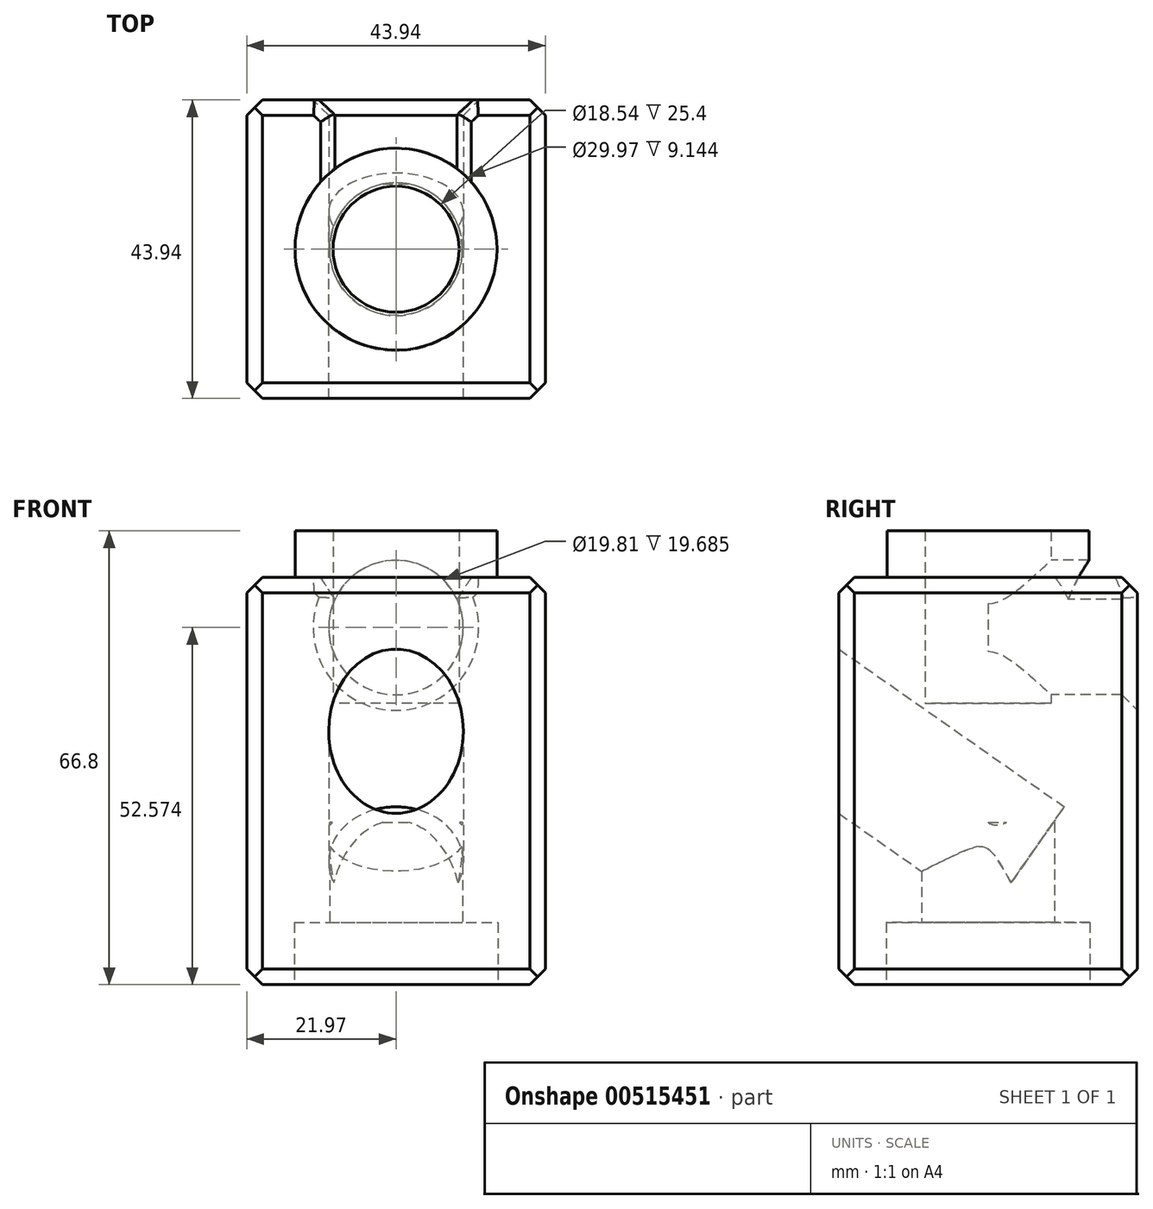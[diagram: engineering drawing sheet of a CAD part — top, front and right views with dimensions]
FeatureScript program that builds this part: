
annotation { "Feature Type Name" : "Feature", "Feature Type Description" : "" }
export const myFeature = defineFeature(function(context is Context, id is Id, definition is map)
    precondition{}
    {
        {
            var Q0;
            Q0=qCreatedBy(makeId("Top.planeOp"),FACE);
            var sketch = newSketch(context, id + "F0", { "sketchPlane" : qUnion([Q0])});
            skCircle(sketch, "E0", {"center": v(0, 0) * mm, "radius": 14.86 * mm});
            skCircle(sketch, "E1", {"center": v(0, 0) * mm, "radius": 9.27 * mm});
            skSolve(sketch);
        }
        {
            var Q0;
            Q0 = qSketchRegion(id + "F0", true);
            extrude(context, id + "F1", {"entities" : qUnion([Q0]), "depth" : 6.86 * mm, "offsetDistance" : 25.4 * mm});
        }
        {
            var Q0;
            Q0=qCreatedBy(makeId("Top.planeOp"),FACE);
            var sketch = newSketch(context, id + "F2", { "sketchPlane" : qUnion([Q0])});
            skLineSegment(sketch, "E2.bottom", {"start": v(-21.97, 21.97) * mm, "end": v(21.97, 21.97) * mm});
            skLineSegment(sketch, "E2.top", {"start": v(-21.97, -21.97) * mm, "end": v(21.97, -21.97) * mm});
            skLineSegment(sketch, "E2.left", {"start": v(-21.97, 21.97) * mm, "end": v(-21.97, -21.97) * mm});
            skLineSegment(sketch, "E2.right", {"start": v(21.97, 21.97) * mm, "end": v(21.97, -21.97) * mm});
            skPoint(sketch, "E2.middle", {"position": v(0, 0) * mm});
            skSolve(sketch);
        }
        {
            var Q0;
            Q0 = qSketchRegion(id + "F2", true);
            extrude(context, id + "F3", {"entities" : qUnion([Q0]), "operationType" : NewBodyOperationType.ADD, "oppositeDirection" : true, "depth" : 59.94 * mm, "offsetDistance" : 25.4 * mm});
        }
        {
            var Q0;
            Q0=makeQuery(id+"F3.boolean.opBoolean","SPLIT",FACE,{"disambiguationData":[TD([makeQuery(id+"F1.opExtrude","SWEPT_FACE",FACE,{"disambiguationData":[OSD([sQuery(id+"F0.wireOp",EDGE,"E1")])]})])],"derivedFrom":makeQuery(id+"F3.opExtrude","CAP_FACE",FACE,{"disambiguationData":[OSD([sQuery(id+"F2.wireOp",EDGE,"E2.bottom"),sQuery(id+"F2.wireOp",EDGE,"E2.top"),sQuery(id+"F2.wireOp",EDGE,"E2.left"),sQuery(id+"F2.wireOp",EDGE,"E2.right")])],"isStart":true})});
            extrude(context, id + "F4", {"entities" : qUnion([Q0]), "operationType" : NewBodyOperationType.REMOVE, "oppositeDirection" : true, "depth" : 18.54 * mm, "offsetDistance" : 25.4 * mm});
        }
        {
            var Q0;
            Q0=makeQuery(id+"F3.opExtrude","SWEPT_EDGE",EDGE,{"disambiguationData":[OSD([sQuery(id+"F2.wireOp",EDGE,"E2.bottom"),sQuery(id+"F2.wireOp",EDGE,"E2.left")])]});
            chamfer(context, id + "F5", {"entities" : qUnion([Q0]), "width" : 2.3 * mm, "tangentPropagation" : true});
        }
        {
            var Q0;
            Q0=makeQuery(id+"F3.opExtrude","SWEPT_EDGE",EDGE,{"disambiguationData":[OSD([sQuery(id+"F2.wireOp",EDGE,"E2.top"),sQuery(id+"F2.wireOp",EDGE,"E2.left")])]});
            var Q1;
            Q1=makeQuery(id+"F3.opExtrude","SWEPT_EDGE",EDGE,{"disambiguationData":[OSD([sQuery(id+"F2.wireOp",EDGE,"E2.bottom"),sQuery(id+"F2.wireOp",EDGE,"E2.right")])]});
            chamfer(context, id + "F6", {"entities" : qUnion([Q0, Q1]), "width" : 2.3 * mm, "tangentPropagation" : true});
        }
        {
            var Q0;
            Q0=makeQuery(id+"F3.opExtrude","SWEPT_EDGE",EDGE,{"disambiguationData":[OSD([sQuery(id+"F2.wireOp",EDGE,"E2.top"),sQuery(id+"F2.wireOp",EDGE,"E2.right")])]});
            chamfer(context, id + "F7", {"entities" : qUnion([Q0]), "width" : 2.3 * mm, "tangentPropagation" : true});
        }
        {
            var Q0;
            Q0=qCreatedBy(makeId("Front.planeOp"),FACE);
            var sketch = newSketch(context, id + "F8", { "sketchPlane" : qUnion([Q0])});
            skCircle(sketch, "E3", {"center": v(0, -7.37) * mm, "radius": 9.9 * mm});
            skSolve(sketch);
        }
        {
            var Q0;
            Q0 = qSketchRegion(id + "F8", true);
            extrude(context, id + "F9", {"entities" : qUnion([Q0]), "operationType" : NewBodyOperationType.REMOVE, "oppositeDirection" : true, "depth" : 25.4 * mm, "offsetDistance" : 25.4 * mm});
        }
        {
            var Q0;
            Q0=makeQuery(id+"F9.boolean.opBoolean","INTERSECT",EDGE,{"derivedFrom":[makeQuery(id+"F3.opExtrude","SWEPT_FACE",FACE,{"disambiguationData":[OSD([sQuery(id+"F2.wireOp",EDGE,"E2.bottom")])]}),makeQuery(id+"F9.opExtrude","SWEPT_FACE",FACE,{"disambiguationData":[OSD([sQuery(id+"F8.wireOp",EDGE,"E3")])]})]});
            chamfer(context, id + "F10", {"entities" : qUnion([Q0]), "width" : 2.3 * mm, "tangentPropagation" : true});
        }
        {
            var Q0;
            {var subQ0=sQuery(id+"F2.wireOp",EDGE,"E2.left");var subQ1=sQuery(id+"F2.wireOp",EDGE,"E2.top");var subQ2=sQuery(id+"F2.wireOp",EDGE,"E2.bottom");var subQ3=sQuery(id+"F2.wireOp",EDGE,"E2.right");Q0=makeQuery(id+"F9.boolean.opBoolean","INTERSECT",EDGE,{"disambiguationData":[OD(1.0)],"derivedFrom":[makeQuery(id+"F3.boolean.opBoolean","SPLIT",FACE,{"disambiguationData":[TD([makeQuery(id+"F1.opExtrude","SWEPT_FACE",FACE,{"disambiguationData":[OSD([sQuery(id+"F0.wireOp",EDGE,"E0")])]})])],"derivedFrom":makeQuery(id+"F3.opExtrude","CAP_FACE",FACE,{"disambiguationData":[OSD([subQ2,subQ1,subQ0,subQ3])],"isStart":true})}),makeQuery(id+"F9.opExtrude","SWEPT_FACE",FACE,{"disambiguationData":[OSD([sQuery(id+"F8.wireOp",EDGE,"E3")])]})]});}
            var Q1;
            {var subQ0=sQuery(id+"F2.wireOp",EDGE,"E2.left");var subQ1=sQuery(id+"F2.wireOp",EDGE,"E2.top");var subQ2=sQuery(id+"F2.wireOp",EDGE,"E2.bottom");var subQ3=sQuery(id+"F2.wireOp",EDGE,"E2.right");Q1=makeQuery(id+"F9.boolean.opBoolean","INTERSECT",EDGE,{"disambiguationData":[OD(0.0)],"derivedFrom":[makeQuery(id+"F3.boolean.opBoolean","SPLIT",FACE,{"disambiguationData":[TD([makeQuery(id+"F1.opExtrude","SWEPT_FACE",FACE,{"disambiguationData":[OSD([sQuery(id+"F0.wireOp",EDGE,"E0")])]})])],"derivedFrom":makeQuery(id+"F3.opExtrude","CAP_FACE",FACE,{"disambiguationData":[OSD([subQ2,subQ1,subQ0,subQ3])],"isStart":true})}),makeQuery(id+"F9.opExtrude","SWEPT_FACE",FACE,{"disambiguationData":[OSD([sQuery(id+"F8.wireOp",EDGE,"E3")])]})]});}
            var Q2;
            {var subQ0=sQuery(id+"F2.wireOp",EDGE,"E2.left");var subQ1=sQuery(id+"F2.wireOp",EDGE,"E2.top");var subQ2=sQuery(id+"F2.wireOp",EDGE,"E2.bottom");var subQ3=makeQuery(id+"F3.opExtrude","SWEPT_FACE",FACE,{"disambiguationData":[OSD([subQ2])]});var subQ4=sQuery(id+"F2.wireOp",EDGE,"E2.right");Q2=makeQuery(id+"F10.opChamfer","BLEND_EDGE",EDGE,{"disambiguationData":[OD(0.0)],"blendedFrom":[makeQuery(id+"F9.boolean.opBoolean","INTERSECT",EDGE,{"derivedFrom":[subQ3,makeQuery(id+"F9.opExtrude","SWEPT_FACE",FACE,{"disambiguationData":[OSD([sQuery(id+"F8.wireOp",EDGE,"E3")])]})]}),makeQuery(id+"F3.boolean.opBoolean","SPLIT",FACE,{"disambiguationData":[TD([makeQuery(id+"F1.opExtrude","SWEPT_FACE",FACE,{"disambiguationData":[OSD([sQuery(id+"F0.wireOp",EDGE,"E0")])]})])],"derivedFrom":makeQuery(id+"F3.opExtrude","CAP_FACE",FACE,{"disambiguationData":[OSD([subQ2,subQ1,subQ0,subQ4])],"isStart":true})})],"blendedInto":[makeQuery(id+"F3.boolean.opBoolean","SPLIT",FACE,{"disambiguationData":[TD([makeQuery(id+"F1.opExtrude","SWEPT_FACE",FACE,{"disambiguationData":[OSD([sQuery(id+"F0.wireOp",EDGE,"E0")])]})])],"derivedFrom":makeQuery(id+"F3.opExtrude","CAP_FACE",FACE,{"disambiguationData":[OSD([subQ2,subQ1,subQ0,subQ4])],"isStart":true})})]});}
            var Q3;
            {var subQ0=sQuery(id+"F2.wireOp",EDGE,"E2.left");var subQ1=sQuery(id+"F2.wireOp",EDGE,"E2.top");var subQ2=sQuery(id+"F2.wireOp",EDGE,"E2.bottom");var subQ3=makeQuery(id+"F3.opExtrude","SWEPT_FACE",FACE,{"disambiguationData":[OSD([subQ2])]});var subQ4=sQuery(id+"F2.wireOp",EDGE,"E2.right");Q3=makeQuery(id+"F10.opChamfer","BLEND_EDGE",EDGE,{"disambiguationData":[OD(1.0)],"blendedFrom":[makeQuery(id+"F9.boolean.opBoolean","INTERSECT",EDGE,{"derivedFrom":[subQ3,makeQuery(id+"F9.opExtrude","SWEPT_FACE",FACE,{"disambiguationData":[OSD([sQuery(id+"F8.wireOp",EDGE,"E3")])]})]}),makeQuery(id+"F3.boolean.opBoolean","SPLIT",FACE,{"disambiguationData":[TD([makeQuery(id+"F1.opExtrude","SWEPT_FACE",FACE,{"disambiguationData":[OSD([sQuery(id+"F0.wireOp",EDGE,"E0")])]})])],"derivedFrom":makeQuery(id+"F3.opExtrude","CAP_FACE",FACE,{"disambiguationData":[OSD([subQ2,subQ1,subQ0,subQ4])],"isStart":true})})],"blendedInto":[makeQuery(id+"F3.boolean.opBoolean","SPLIT",FACE,{"disambiguationData":[TD([makeQuery(id+"F1.opExtrude","SWEPT_FACE",FACE,{"disambiguationData":[OSD([sQuery(id+"F0.wireOp",EDGE,"E0")])]})])],"derivedFrom":makeQuery(id+"F3.opExtrude","CAP_FACE",FACE,{"disambiguationData":[OSD([subQ2,subQ1,subQ0,subQ4])],"isStart":true})})]});}
            chamfer(context, id + "F11", {"entities" : qUnion([Q0, Q1, Q2, Q3]), "width" : 2.3 * mm, "tangentPropagation" : true});
        }
        {
            var Q0;
            Q0=qCreatedBy(makeId("Top.planeOp"),FACE);
            var sketch = newSketch(context, id + "F12", { "sketchPlane" : qUnion([Q0])});
            skCircle(sketch, "E4", {"center": v(0, 0) * mm, "radius": 15.13 * mm});
            skCircle(sketch, "E5", {"center": v(0, 0) * mm, "radius": 9.78 * mm});
            skSolve(sketch);
        }
        {
            var Q0;
            Q0=makeQuery(id+"F3.opExtrude","CAP_FACE",FACE,{"disambiguationData":[OSD([sQuery(id+"F2.wireOp",EDGE,"E2.bottom"),sQuery(id+"F2.wireOp",EDGE,"E2.top"),sQuery(id+"F2.wireOp",EDGE,"E2.left"),sQuery(id+"F2.wireOp",EDGE,"E2.right")])],"isStart":false});
            var sketch = newSketch(context, id + "F13", { "sketchPlane" : qUnion([Q0])});
            skCircle(sketch, "E6", {"center": v(0, 0) * mm, "radius": 14.99 * mm});
            skCircle(sketch, "E7", {"center": v(0, 0) * mm, "radius": 9.78 * mm});
            skSolve(sketch);
        }
        {
            var Q0;
            Q0 = qSketchRegion(id + "F13", true);
            extrude(context, id + "F14", {"entities" : qUnion([Q0]), "operationType" : NewBodyOperationType.REMOVE, "oppositeDirection" : true, "depth" : 9.14 * mm, "offsetDistance" : 25.4 * mm});
        }
        {
            var Q0;
            Q0=qCreatedBy(makeId("Top.planeOp"),FACE);
            var sketch = newSketch(context, id + "F15", { "sketchPlane" : qUnion([Q0])});
            skSolve(sketch);
        }
        {
            var Q0;
            Q0 = qSketchRegion(id + "F15", true);
            var Q1;
            Q1=makeQuery(id+"F14.boolean.opBoolean","SPLIT",FACE,{"disambiguationData":[TD([makeQuery(id+"F14.opExtrude","SWEPT_FACE",FACE,{"disambiguationData":[OSD([sQuery(id+"F13.wireOp",EDGE,"E7")])]})])],"derivedFrom":makeQuery(id+"F3.opExtrude","CAP_FACE",FACE,{"disambiguationData":[OSD([sQuery(id+"F2.wireOp",EDGE,"E2.bottom"),sQuery(id+"F2.wireOp",EDGE,"E2.top"),sQuery(id+"F2.wireOp",EDGE,"E2.left"),sQuery(id+"F2.wireOp",EDGE,"E2.right")])],"isStart":false})});
            extrude(context, id + "F16", {"entities" : qUnion([Q0, Q1]), "operationType" : NewBodyOperationType.REMOVE, "oppositeDirection" : true, "depth" : 23.88 * mm, "offsetDistance" : 25.4 * mm});
        }
        {
            var Q0;
            Q0=makeQuery(id+"F3.opExtrude","CAP_EDGE",EDGE,{"disambiguationData":[OSD([sQuery(id+"F2.wireOp",EDGE,"E2.top")])],"isStart":false});
            var Q1;
            Q1=makeQuery(id+"F3.opExtrude","CAP_EDGE",EDGE,{"disambiguationData":[OSD([sQuery(id+"F2.wireOp",EDGE,"E2.left")])],"isStart":false});
            var Q2;
            Q2=makeQuery(id+"F3.opExtrude","CAP_EDGE",EDGE,{"disambiguationData":[OSD([sQuery(id+"F2.wireOp",EDGE,"E2.bottom")])],"isStart":false});
            var Q3;
            Q3=makeQuery(id+"F3.opExtrude","CAP_EDGE",EDGE,{"disambiguationData":[OSD([sQuery(id+"F2.wireOp",EDGE,"E2.right")])],"isStart":false});
            chamfer(context, id + "F17", {"entities" : qUnion([Q0, Q1, Q2, Q3]), "width" : 2.3 * mm, "tangentPropagation" : true});
        }
        {
            var Q0;
            Q0=makeQuery(id+"F3.opExtrude","SWEPT_FACE",FACE,{"disambiguationData":[OSD([sQuery(id+"F2.wireOp",EDGE,"E2.top")])]});
            var sketch = newSketch(context, id + "F18", { "sketchPlane" : qUnion([Q0])});
            skCircle(sketch, "E8", {"center": v(0, -28.96) * mm, "radius": 9.9 * mm});
            skSolve(sketch);
        }
        {
            var Q0;
            Q0=makeQuery(id+"F18.imprint","IMPRINT",FACE,{"disambiguationData":[TD([[makeQuery(id+"F18.imprint","IMPRINT",EDGE,{"derivedFrom":sQuery(id+"F18.wireOp",EDGE,"E8")}),1.0]])]});
            var Q1;
            Q1=sQuery(id+"F18.wireOp",EDGE,"E8");
            extrude(context, id + "F19", {"entities" : qUnion([Q0]), "surfaceEntities" : qUnion([Q1]), "depth" : 3.8 * mm, "offsetDistance" : 25.4 * mm});
        }
        {
            var Q0;
            Q0=makeQuery(id+"F19.opExtrude","SWEPT_BODY",BODY,{"disambiguationData":[OSD([sQuery(id+"F18.wireOp",EDGE,"E8")])]});
            var Q1;
            {var subQ0=sQuery(id+"F2.wireOp",EDGE,"E2.top");Q1=makeQuery(id+"F17.opChamfer","BLEND_EDGE",EDGE,{"blendedFrom":[makeQuery(id+"F3.opExtrude","CAP_EDGE",EDGE,{"disambiguationData":[OSD([subQ0])],"isStart":false}),makeQuery(id+"F3.opExtrude","SWEPT_FACE",FACE,{"disambiguationData":[OSD([subQ0])]})],"blendedInto":[makeQuery(id+"F3.opExtrude","SWEPT_FACE",FACE,{"disambiguationData":[OSD([subQ0])]})]});}
            transform(context, id + "F20", {"entities" : qUnion([Q0]), "transformType" : TransformType.ROTATION, "transformAxis" : qUnion([Q1]), "angle" : 35 * degree, "oppositeDirection" : true, "makeCopy" : false});
        }
        {
            var Q0;
            Q0=makeQuery(id+"F19.opExtrude","CAP_FACE",FACE,{"disambiguationData":[OSD([sQuery(id+"F18.wireOp",EDGE,"E8")])],"isStart":true});
            extrude(context, id + "F21", {"entities" : qUnion([Q0]), "depth" : 13.46 * mm, "offsetDistance" : 25.4 * mm});
        }
        {
            var Q0;
            Q0=makeQuery(id+"F19.opExtrude","CAP_FACE",FACE,{"disambiguationData":[OSD([sQuery(id+"F18.wireOp",EDGE,"E8")])],"isStart":false});
            var Q1;
            Q1=makeQuery(id+"F21.opExtrude","CAP_FACE",FACE,{"disambiguationData":[OSD([sQuery(id+"F18.wireOp",EDGE,"E8")])],"isStart":false});
            extrude(context, id + "F22", {"entities" : qUnion([Q0, Q1]), "operationType" : NewBodyOperationType.REMOVE, "depth" : 35.05 * mm, "offsetDistance" : 25.4 * mm});
        }
        {
            var Q0;
            Q0=makeQuery(id+"F3.opExtrude","CAP_EDGE",EDGE,{"disambiguationData":[OSD([sQuery(id+"F2.wireOp",EDGE,"E2.left")])],"isStart":true});
            var Q1;
            Q1=makeQuery(id+"F3.opExtrude","CAP_EDGE",EDGE,{"disambiguationData":[OSD([sQuery(id+"F2.wireOp",EDGE,"E2.top")])],"isStart":true});
            var Q2;
            Q2=makeQuery(id+"F3.opExtrude","CAP_EDGE",EDGE,{"disambiguationData":[OSD([sQuery(id+"F2.wireOp",EDGE,"E2.right")])],"isStart":true});
            var Q3;
            {var subQ0=sQuery(id+"F2.wireOp",EDGE,"E2.bottom");var subQ1=sQuery(id+"F2.wireOp",EDGE,"E2.right");Q3=makeQuery(id+"F9.boolean.opBoolean","SPLIT",EDGE,{"disambiguationData":[TD([makeQuery(id+"F6.opChamfer","BLEND_FACE",FACE,{"disambiguationData":[OSD([subQ0,subQ1])]})])],"derivedFrom":makeQuery(id+"F3.opExtrude","CAP_EDGE",EDGE,{"disambiguationData":[OSD([subQ0])],"isStart":true})});}
            var Q4;
            {var subQ0=sQuery(id+"F2.wireOp",EDGE,"E2.bottom");var subQ1=sQuery(id+"F2.wireOp",EDGE,"E2.left");Q4=makeQuery(id+"F9.boolean.opBoolean","SPLIT",EDGE,{"disambiguationData":[TD([makeQuery(id+"F5.opChamfer","BLEND_FACE",FACE,{"disambiguationData":[OSD([subQ0,subQ1])]})])],"derivedFrom":makeQuery(id+"F3.opExtrude","CAP_EDGE",EDGE,{"disambiguationData":[OSD([subQ0])],"isStart":true})});}
            chamfer(context, id + "F23", {"entities" : qUnion([Q0, Q1, Q2, Q3, Q4]), "width" : 2.3 * mm, "tangentPropagation" : true});
        }
    });
